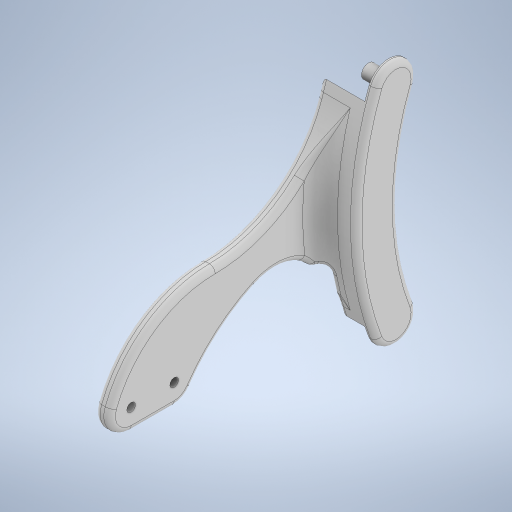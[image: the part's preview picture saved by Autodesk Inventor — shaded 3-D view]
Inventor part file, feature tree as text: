
AUTODESK INVENTOR PART (.ipt)
format: ipt  version: 2023 (Build 270158000, 158)  size: 508,416 bytes
history: native  units: mm
features: other x6, extrude x5, sketch x2, fillet x1
ambient origin geometry x8: Origin, YZ Plane, XZ Plane, XY Plane, X Axis, Y Axis, Z Axis, Center Point
bodies: Body1 (feature_tree)
feature tree (14):
  other  "Sólido1"
  sketch  "Boceto1"  dims[d0=100.0mm d1=85.0mm]
  extrude  "Extrusión1"  Depth=85.0mm
  extrude  "Extrusión2"  Depth=1.74mm
  extrude  "Extrusión4"  Depth=1.74mm
  extrude  "Extrusión5"  Depth=1.74mm
  other  "Empalme de cara1"
  other  "Empalme de cara2"
  fillet  "Empalme1"  Radius=15.0mm
  extrude  "Extrusión6"  Depth=1.74mm
  other  "Empalme de cara3"
  other  "Empalme de cara4"
  other  "Empalme de cara5"
  sketch  "Boceto2"  dims[d2=70.5mm d3=7.25mm d4=7.25mm d5=14.9mm d6=15.0mm d7=157.0mm d8=4.9mm d9=7.0mm d10=0.0mm d11=8.0mm d12=2.5mm d13=0.0mm d14=1.0mm d17=10.0mm d18=10.0mm d19=23.0mm d20=10.0mm d22=3.0mm d23=110.0mm d24=15.0mm d25=0.0mm d26=10.0mm d27=0.0mm d28=17.0mm d29=6.0mm d30=2.0mm d31=17.0mm d32=7.0mm d33=10.0mm d34=0.0mm d35=2.47mm d36=2.47mm d37=1.74mm]
